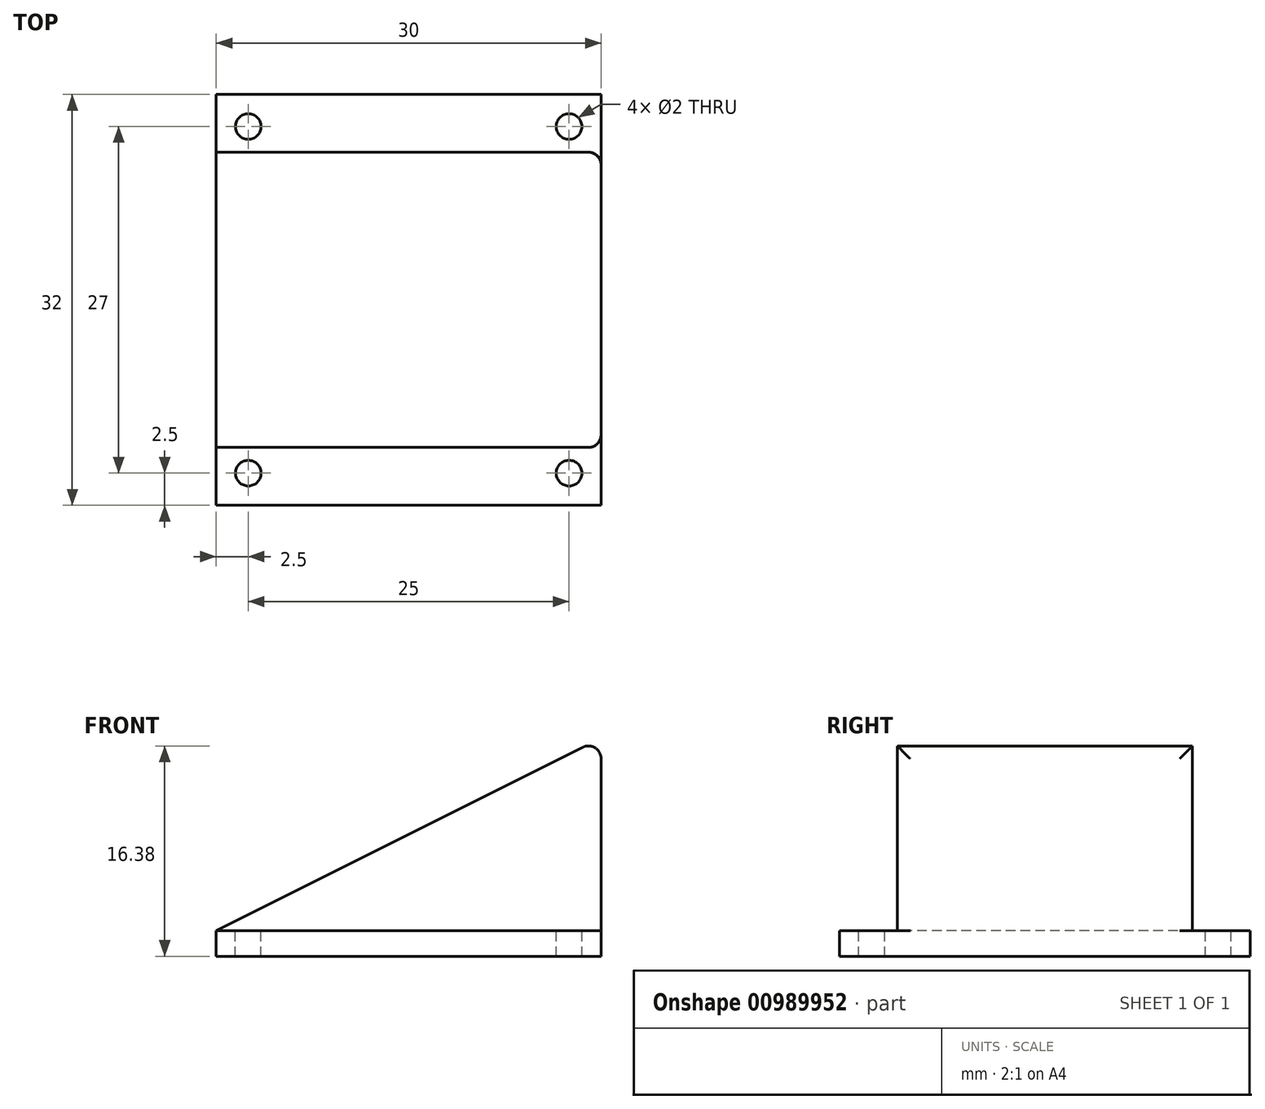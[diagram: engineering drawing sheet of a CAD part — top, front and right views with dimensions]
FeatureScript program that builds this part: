
annotation { "Feature Type Name" : "Feature", "Feature Type Description" : "" }
export const myFeature = defineFeature(function(context is Context, id is Id, definition is map)
    precondition{}
    {
        {
            var Q0;
            Q0=qCreatedBy(makeId("Top.planeOp"),FACE);
            var sketch = newSketch(context, id + "F0", { "sketchPlane" : qUnion([Q0])});
            skLineSegment(sketch, "E0.bottom", {"start": v(-15, 16) * mm, "end": v(15, 16) * mm});
            skLineSegment(sketch, "E0.top", {"start": v(-15, -16) * mm, "end": v(15, -16) * mm});
            skLineSegment(sketch, "E0.left", {"start": v(-15, 16) * mm, "end": v(-15, -16) * mm});
            skLineSegment(sketch, "E0.right", {"start": v(15, 16) * mm, "end": v(15, -16) * mm});
            skSolve(sketch);
        }
        {
            var Q0;
            Q0=makeQuery(id+"F0.imprint","IMPRINT",FACE,{"disambiguationData":[TD([[makeQuery(id+"F0.imprint","IMPRINT",EDGE,{"derivedFrom":sQuery(id+"F0.wireOp",EDGE,"E0.bottom")}),-1.0]])]});
            extrude(context, id + "F1", {"entities" : qUnion([Q0]), "depth" : 2 * mm, "offsetDistance" : 25 * mm});
        }
        {
            var Q0;
            Q0=makeQuery(id+"F1.opExtrude","CAP_FACE",FACE,{"disambiguationData":[OSD([sQuery(id+"F0.wireOp",EDGE,"E0.bottom"),sQuery(id+"F0.wireOp",EDGE,"E0.top"),sQuery(id+"F0.wireOp",EDGE,"E0.left"),sQuery(id+"F0.wireOp",EDGE,"E0.right")])],"isStart":false});
            var sketch = newSketch(context, id + "F2", { "sketchPlane" : qUnion([Q0])});
            skCircle(sketch, "E1", {"center": v(-12.5, 13.5) * mm, "radius": 1 * mm});
            skCircle(sketch, "E2", {"center": v(12.5, 13.5) * mm, "radius": 1 * mm});
            skCircle(sketch, "E3", {"center": v(12.5, -13.5) * mm, "radius": 1 * mm});
            skCircle(sketch, "E4", {"center": v(-12.5, -13.5) * mm, "radius": 1 * mm});
            skSolve(sketch);
        }
        {
            var Q0;
            Q0=makeQuery(id+"F2.imprint","IMPRINT",FACE,{"disambiguationData":[TD([[makeQuery(id+"F2.imprint","IMPRINT",EDGE,{"derivedFrom":sQuery(id+"F2.wireOp",EDGE,"E2")}),1.0]])]});
            var Q1;
            Q1=makeQuery(id+"F2.imprint","IMPRINT",FACE,{"disambiguationData":[TD([[makeQuery(id+"F2.imprint","IMPRINT",EDGE,{"derivedFrom":sQuery(id+"F2.wireOp",EDGE,"E1")}),1.0]])]});
            var Q2;
            Q2=makeQuery(id+"F2.imprint","IMPRINT",FACE,{"disambiguationData":[TD([[makeQuery(id+"F2.imprint","IMPRINT",EDGE,{"derivedFrom":sQuery(id+"F2.wireOp",EDGE,"E4")}),1.0]])]});
            var Q3;
            Q3=makeQuery(id+"F2.imprint","IMPRINT",FACE,{"disambiguationData":[TD([[makeQuery(id+"F2.imprint","IMPRINT",EDGE,{"derivedFrom":sQuery(id+"F2.wireOp",EDGE,"E3")}),1.0]])]});
            extrude(context, id + "F3", {"entities" : qUnion([Q0, Q1, Q2, Q3]), "operationType" : NewBodyOperationType.REMOVE, "oppositeDirection" : true, "depth" : 2 * mm, "offsetDistance" : 25 * mm});
        }
        {
            var Q0;
            Q0=makeQuery(id+"F1.opExtrude","CAP_FACE",FACE,{"disambiguationData":[OSD([sQuery(id+"F0.wireOp",EDGE,"E0.bottom"),sQuery(id+"F0.wireOp",EDGE,"E0.top"),sQuery(id+"F0.wireOp",EDGE,"E0.left"),sQuery(id+"F0.wireOp",EDGE,"E0.right")])],"isStart":false});
            var sketch = newSketch(context, id + "F4", { "sketchPlane" : qUnion([Q0])});
            skLineSegment(sketch, "E5.bottom", {"start": v(15, 11.5) * mm, "end": v(-15, 11.5) * mm});
            skLineSegment(sketch, "E5.top", {"start": v(15, -11.5) * mm, "end": v(-15, -11.5) * mm});
            skLineSegment(sketch, "E5.left", {"start": v(15, 11.5) * mm, "end": v(15, -11.5) * mm});
            skLineSegment(sketch, "E5.right", {"start": v(-15, 11.5) * mm, "end": v(-15, -11.5) * mm});
            skSolve(sketch);
        }
        {
            var Q0;
            Q0=makeQuery(id+"F4.imprint","IMPRINT",FACE,{"disambiguationData":[TD([[makeQuery(id+"F4.imprint","IMPRINT",EDGE,{"derivedFrom":sQuery(id+"F4.wireOp",EDGE,"E5.bottom")}),1.0]])]});
            extrude(context, id + "F5", {"entities" : qUnion([Q0]), "operationType" : NewBodyOperationType.ADD, "depth" : 15 * mm, "offsetDistance" : 25 * mm});
        }
        {
            var Q0;
            Q0=makeQuery(id+"F5.opExtrude","SWEPT_FACE",FACE,{"disambiguationData":[OSD([sQuery(id+"F4.wireOp",EDGE,"E5.top")])]});
            var sketch = newSketch(context, id + "F6", { "sketchPlane" : qUnion([Q0])});
            skLineSegment(sketch, "E6", {"start": v(15, 17) * mm, "end": v(-15, 2) * mm});
            skLineSegment(sketch, "E7", {"start": v(-15, 2) * mm, "end": v(-15, 17) * mm});
            skLineSegment(sketch, "E8", {"start": v(-15, 17) * mm, "end": v(15, 17) * mm});
            skSolve(sketch);
        }
        {
            var Q0;
            Q0=makeQuery(id+"F6.imprint","IMPRINT",FACE,{"disambiguationData":[TD([[makeQuery(id+"F6.imprint","IMPRINT",EDGE,{"derivedFrom":sQuery(id+"F6.wireOp",EDGE,"E6")}),-1.0]])]});
            extrude(context, id + "F7", {"entities" : qUnion([Q0]), "operationType" : NewBodyOperationType.REMOVE, "oppositeDirection" : true, "depth" : 23 * mm, "offsetDistance" : 25 * mm});
        }
        {
            var Q0;
            Q0=makeQuery(id+"F5.opExtrude","SWEPT_EDGE",EDGE,{"disambiguationData":[OSD([sQuery(id+"F0.wireOp",EDGE,"E0.right"),sQuery(id+"F4.wireOp",EDGE,"E5.top"),sQuery(id+"F4.wireOp",EDGE,"E5.left")])]});
            var Q1;
            {var subQ0=sQuery(id+"F4.wireOp",EDGE,"E5.left");Q1=makeQuery(id+"F7.boolean.opBoolean","MERGE",EDGE,{"derivedFrom":[makeQuery(id+"F5.opExtrude","CAP_EDGE",EDGE,{"disambiguationData":[OSD([subQ0])],"isStart":false})],"fromTools":[makeQuery(id+"F7.opExtrude","SWEPT_EDGE",EDGE,{"disambiguationData":[OSD([sQuery(id+"F0.wireOp",EDGE,"E0.right"),sQuery(id+"F4.wireOp",EDGE,"E5.top"),subQ0,sQuery(id+"F6.wireOp",EDGE,"E6"),sQuery(id+"F6.wireOp",EDGE,"E8")])]})]});}
            var Q2;
            Q2=makeQuery(id+"F7.boolean.opBoolean","COPY",EDGE,{"derivedFrom":makeQuery(id+"F7.opExtrude","CAP_EDGE",EDGE,{"disambiguationData":[OSD([sQuery(id+"F6.wireOp",EDGE,"E6")])],"isStart":true})});
            var Q3;
            Q3=makeQuery(id+"F5.opExtrude","SWEPT_EDGE",EDGE,{"disambiguationData":[OSD([sQuery(id+"F0.wireOp",EDGE,"E0.right"),sQuery(id+"F4.wireOp",EDGE,"E5.bottom"),sQuery(id+"F4.wireOp",EDGE,"E5.left")])]});
            var Q4;
            Q4=makeQuery(id+"F7.boolean.opBoolean","COPY",EDGE,{"derivedFrom":makeQuery(id+"F7.opExtrude","CAP_EDGE",EDGE,{"disambiguationData":[OSD([sQuery(id+"F6.wireOp",EDGE,"E6")])],"isStart":false})});
            fillet(context, id + "F8", {"entities" : qUnion([Q0, Q1, Q2, Q3, Q4]), "radius" : 1 * mm, "tangentPropagation" : true, "allowEdgeOverflow" : false});
        }
    });
